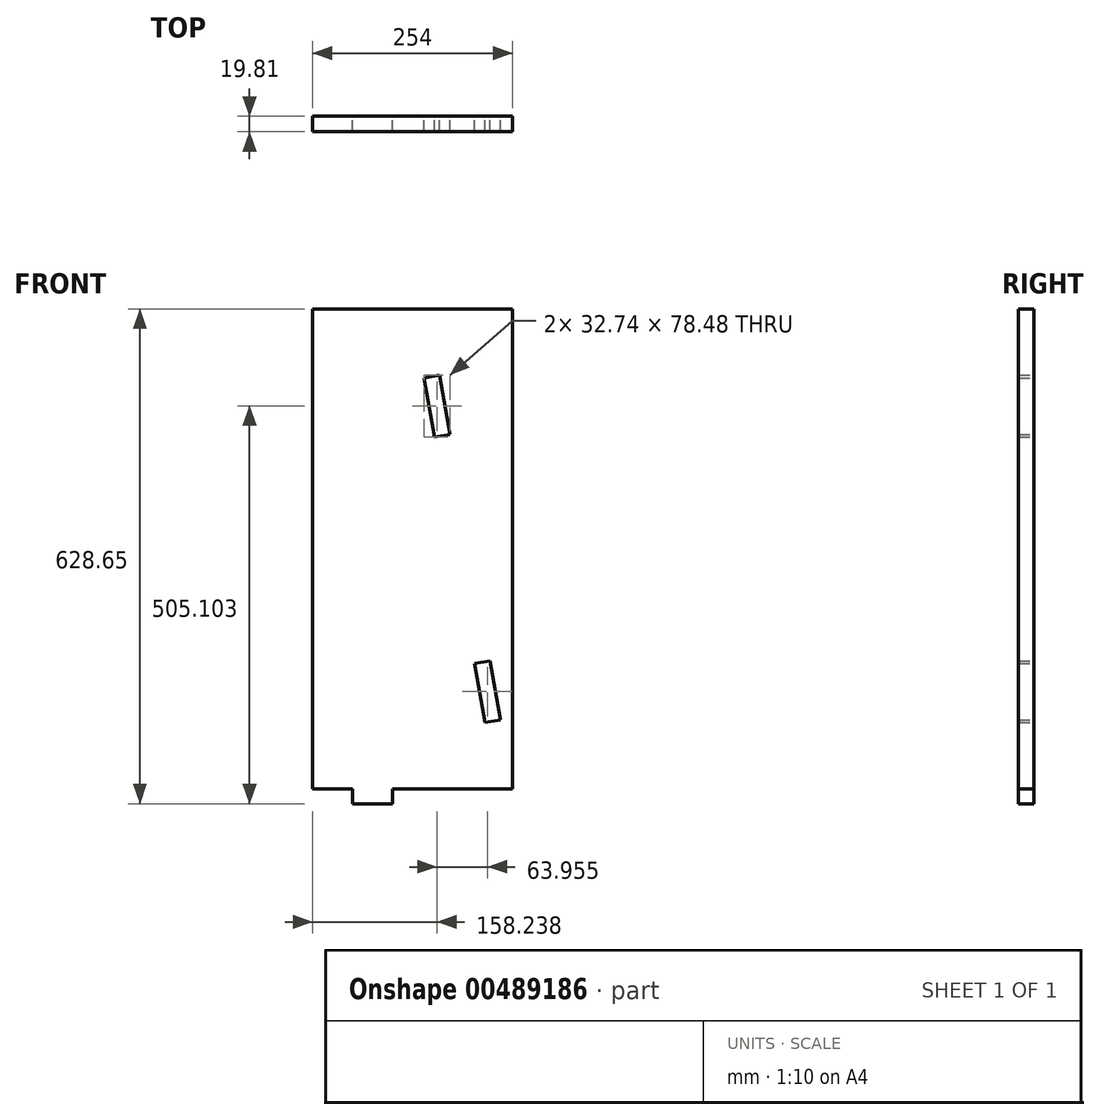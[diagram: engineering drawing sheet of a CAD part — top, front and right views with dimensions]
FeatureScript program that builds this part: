
annotation { "Feature Type Name" : "Feature", "Feature Type Description" : "" }
export const myFeature = defineFeature(function(context is Context, id is Id, definition is map)
    precondition{}
    {
        {
            var Q0;
            Q0=qCreatedBy(makeId("Front.planeOp"),FACE);
            var sketch = newSketch(context, id + "F0", { "sketchPlane" : qUnion([Q0])});
            skLineSegment(sketch, "E0.bottom", {"start": v(-14.52, 559.24) * mm, "end": v(239.48, 559.24) * mm});
            skLineSegment(sketch, "E0.top", {"start": v(-14.52, -50.36) * mm, "end": v(239.48, -50.36) * mm});
            skLineSegment(sketch, "E0.left", {"start": v(-14.52, 559.24) * mm, "end": v(-14.52, -50.36) * mm});
            skLineSegment(sketch, "E0.right", {"start": v(239.48, 559.24) * mm, "end": v(239.48, -50.36) * mm});
            skLineSegment(sketch, "E1", {"start": v(36.28, -50.36) * mm, "end": v(36.28, -69.41) * mm});
            skLineSegment(sketch, "E2", {"start": v(36.28, -69.41) * mm, "end": v(87.08, -69.41) * mm});
            skLineSegment(sketch, "E3", {"start": v(87.08, -69.41) * mm, "end": v(87.08, -50.36) * mm});
            skLineSegment(sketch, "E4", {"start": v(87.08, -50.36) * mm, "end": v(36.28, -50.36) * mm});
            skLineSegment(sketch, "E5", {"start": v(188.68, -50.36) * mm, "end": v(137.88, -50.36) * mm});
            skLineSegment(sketch, "E6", {"start": v(137.88, -50.36) * mm, "end": v(137.88, -69.41) * mm});
            skLineSegment(sketch, "E7", {"start": v(137.88, -69.41) * mm, "end": v(188.68, -69.41) * mm});
            skLineSegment(sketch, "E8", {"start": v(188.68, -69.41) * mm, "end": v(188.68, -50.36) * mm});
            skLineSegment(sketch, "E9", {"start": v(219.36, -50.36) * mm, "end": v(113.5, 549.98) * mm});
            skLineSegment(sketch, "E10", {"start": v(224.04, 37.19) * mm, "end": v(204.53, 33.75) * mm});
            skLineSegment(sketch, "E11", {"start": v(204.53, 33.75) * mm, "end": v(191.3, 108.79) * mm});
            skLineSegment(sketch, "E12", {"start": v(127.35, 471.5) * mm, "end": v(146.86, 474.93) * mm});
            skLineSegment(sketch, "E13", {"start": v(146.86, 474.93) * mm, "end": v(160.09, 399.9) * mm});
            skLineSegment(sketch, "E14", {"start": v(160.09, 399.9) * mm, "end": v(140.58, 396.45) * mm});
            skLineSegment(sketch, "E15", {"start": v(140.58, 396.45) * mm, "end": v(127.35, 471.5) * mm});
            skLineSegment(sketch, "E16", {"start": v(219.36, -50.36) * mm, "end": v(239.48, -50.36) * mm});
            skLineSegment(sketch, "E17", {"start": v(133.63, 549.98) * mm, "end": v(239.48, -50.36) * mm});
            skLineSegment(sketch, "E18", {"start": v(113.5, 549.98) * mm, "end": v(133.63, 549.98) * mm});
            skLineSegment(sketch, "E19", {"start": v(191.3, 108.79) * mm, "end": v(210.81, 112.23) * mm});
            skLineSegment(sketch, "E20", {"start": v(210.81, 112.23) * mm, "end": v(224.04, 37.19) * mm});
            skSolve(sketch);
        }
        {
            var Q0;
            Q0=makeQuery(id+"F0.imprint","IMPRINT",FACE,{"disambiguationData":[TD([[makeQuery(id+"F0.imprint","IMPRINT",EDGE,{"derivedFrom":sQuery(id+"F0.wireOp",EDGE,"E0.bottom")}),-1.0]])]});
            var Q1;
            {var subQ0=sQuery(id+"F0.wireOp",EDGE,"IEXf1DnI-W6qj-tIU3-qxrU-LKUCoVdIpDl3");Q1=makeQuery(id+"F0.imprint","IMPRINT",FACE,{"disambiguationData":[TD([[makeQuery(id+"F0.imprint","IMPRINT",EDGE,{"derivedFrom":subQ0}),1.0]])]});}
            var Q2;
            {var subQ0=sQuery(id+"F0.wireOp",EDGE,"X8iBAZjn-jfqn-Oj66-ymr1-2CVGOf5Pt5C7");Q2=makeQuery(id+"F0.imprint","IMPRINT",FACE,{"disambiguationData":[TD([[makeQuery(id+"F0.imprint","IMPRINT",EDGE,{"derivedFrom":subQ0}),-1.0]])]});}
            var Q3;
            {var subQ3=sQuery(id+"F0.wireOp",EDGE,"d1CbcxCj-hZN7-FN1I-Bm9M-C5dE2JiMl6pt");Q3=makeQuery(id+"F0.imprint","IMPRINT",FACE,{"disambiguationData":[TD([[makeQuery(id+"F0.imprint","IMPRINT",EDGE,{"derivedFrom":subQ3}),-1.0]])]});}
            var Q4;
            Q4=makeQuery(id+"F0.imprint","IMPRINT",FACE,{"disambiguationData":[TD([[makeQuery(id+"F0.imprint","IMPRINT",EDGE,{"derivedFrom":sQuery(id+"F0.wireOp",EDGE,"E1")}),1.0]])]});
            var Q5;
            Q5=makeQuery(id+"F0.imprint","IMPRINT",FACE,{"disambiguationData":[TD([[makeQuery(id+"F0.imprint","IMPRINT",EDGE,{"derivedFrom":sQuery(id+"F0.wireOp",EDGE,"E5")}),1.0]])]});
            var Q6;
            {var subQ0=sQuery(id+"F0.wireOp",EDGE,"TRJvLh6X-159q-DYX4-Oluq-1Amk3SQ8fCUs");Q6=makeQuery(id+"F0.imprint","IMPRINT",FACE,{"disambiguationData":[TD([[makeQuery(id+"F0.imprint","IMPRINT",EDGE,{"derivedFrom":subQ0}),-1.0]])]});}
            var Q7;
            {var subQ0=sQuery(id+"F0.wireOp",EDGE,"IuU9qxhL-339i-jZfr-UBv6-JChQLWSCNUk3");Q7=makeQuery(id+"F0.imprint","IMPRINT",FACE,{"disambiguationData":[TD([[makeQuery(id+"F0.imprint","IMPRINT",EDGE,{"derivedFrom":subQ0}),-1.0]])]});}
            var Q8;
            {var subQ0=sQuery(id+"F0.wireOp",EDGE,"bztVRCY3-QFik-BGAe-7fqM-Zr8ZrEfCsVgL");Q8=makeQuery(id+"F0.imprint","IMPRINT",FACE,{"disambiguationData":[TD([[makeQuery(id+"F0.imprint","IMPRINT",EDGE,{"derivedFrom":subQ0}),1.0]])]});}
            var Q9;
            {var subQ5=sQuery(id+"F0.wireOp",EDGE,"85CgDlUa-KM5G-jgX6-XGXF-aFtzrKUNaYqC");Q9=makeQuery(id+"F0.imprint","IMPRINT",FACE,{"disambiguationData":[TD([[makeQuery(id+"F0.imprint","IMPRINT",EDGE,{"derivedFrom":subQ5}),-1.0]])]});}
            var Q10;
            {var subQ0=sQuery(id+"F0.wireOp",EDGE,"E0.right");var subQ1=sQuery(id+"F0.wireOp",EDGE,"E0.top");var subQ2=makeQuery(id+"F0.imprint","INTERSECT",VERTEX,{"derivedFrom":[subQ1,subQ0]});Q10=makeQuery(id+"F0.imprint","IMPRINT",FACE,{"disambiguationData":[TD([[makeQuery(id+"F0.imprint","IMPRINT",EDGE,{"disambiguationData":[TD([[subQ2,1.0]])],"derivedFrom":subQ0}),-1.0]])]});}
            var Q11;
            {var subQ2=sQuery(id+"F0.wireOp",EDGE,"E12");Q11=makeQuery(id+"F0.imprint","IMPRINT",FACE,{"disambiguationData":[TD([[makeQuery(id+"F0.imprint","IMPRINT",EDGE,{"derivedFrom":subQ2}),1.0]])]});}
            var Q12;
            {var subQ0=sQuery(id+"F0.wireOp",EDGE,"Vz6NeczD-1Ss9-Jn3L-virz-QYU8SHH3esIR");Q12=makeQuery(id+"F0.imprint","IMPRINT",FACE,{"disambiguationData":[TD([[makeQuery(id+"F0.imprint","IMPRINT",EDGE,{"derivedFrom":subQ0}),1.0]])]});}
            var Q13;
            {var subQ2=sQuery(id+"F0.wireOp",EDGE,"E10");Q13=makeQuery(id+"F0.imprint","IMPRINT",FACE,{"disambiguationData":[TD([[makeQuery(id+"F0.imprint","IMPRINT",EDGE,{"derivedFrom":subQ2}),1.0]])]});}
            var Q14;
            {var subQ2=sQuery(id+"F0.wireOp",EDGE,"E14");Q14=makeQuery(id+"F0.imprint","IMPRINT",FACE,{"disambiguationData":[TD([[makeQuery(id+"F0.imprint","IMPRINT",EDGE,{"derivedFrom":subQ2}),1.0]])]});}
            extrude(context, id + "F1", {"entities" : qUnion([Q0, Q1, Q2, Q3, Q4, Q5, Q6, Q7, Q8, Q9, Q10, Q11, Q12, Q13, Q14]), "depth" : 19.8 * mm, "offsetDistance" : 25.4 * mm});
        }
    });
